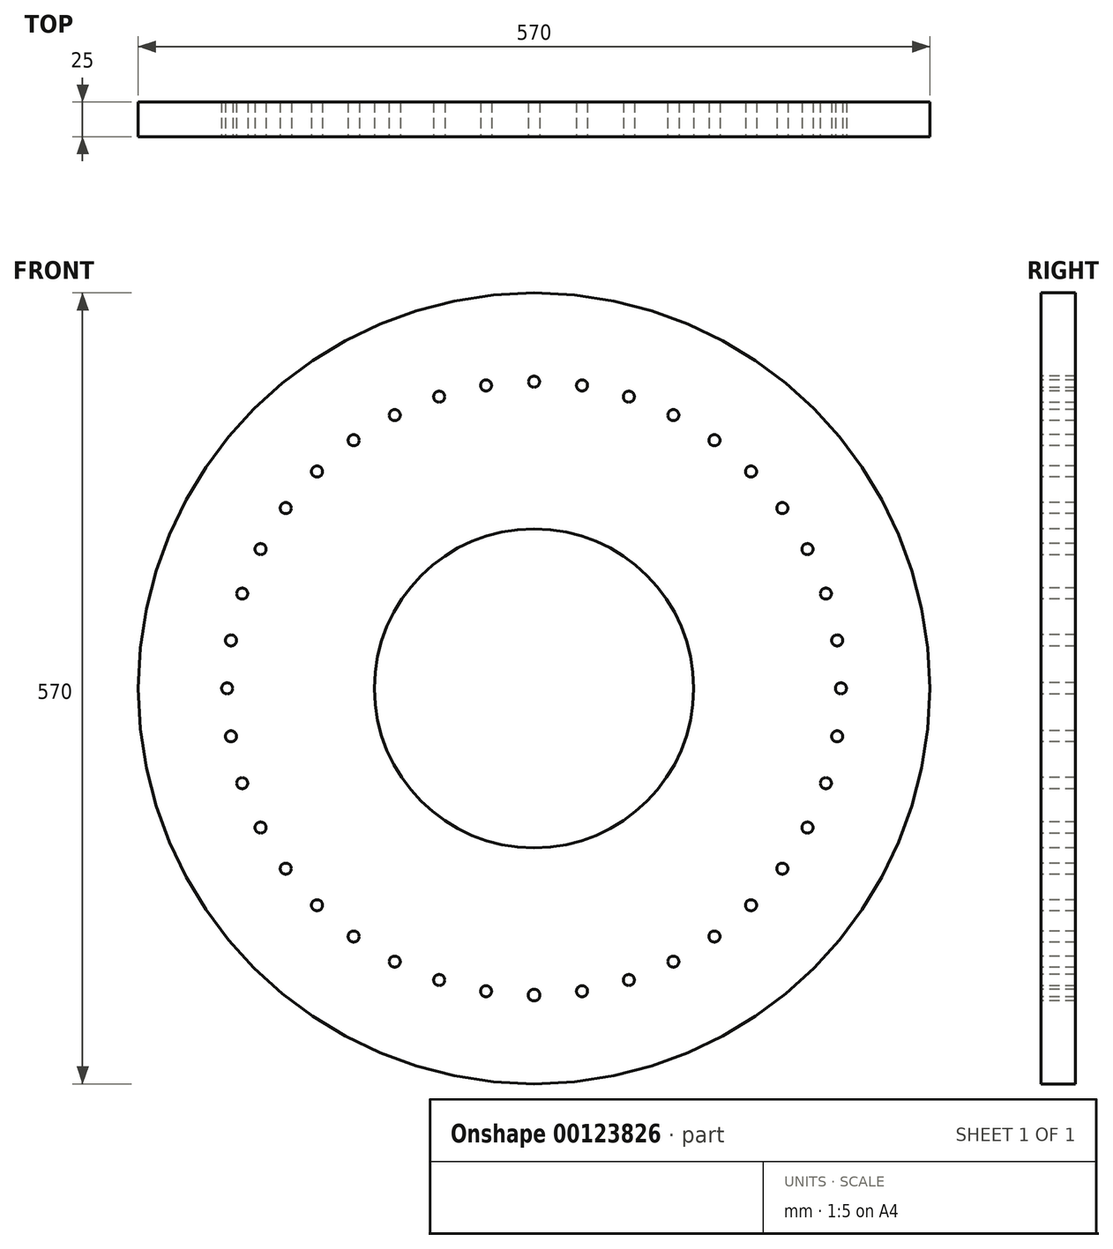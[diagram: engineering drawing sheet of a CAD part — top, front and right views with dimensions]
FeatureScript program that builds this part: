
annotation { "Feature Type Name" : "Feature", "Feature Type Description" : "" }
export const myFeature = defineFeature(function(context is Context, id is Id, definition is map)
    precondition{}
    {
        {
            var Q0;
            Q0=qCreatedBy(makeId("Front.planeOp"),FACE);
            var sketch = newSketch(context, id + "F0", { "sketchPlane" : qUnion([Q0])});
            skCircle(sketch, "E0", {"center": v(0, 0) * mm, "radius": 221 * mm, "construction": true});
            skLineSegment(sketch, "E1", {"start": v(0, 0) * mm, "end": v(0, 221) * mm, "construction": true});
            skLineSegment(sketch, "E2", {"start": v(0, 0) * mm, "end": v(-221, 0) * mm, "construction": true});
            skLineSegment(sketch, "E3", {"start": v(-218.28, 34.57) * mm, "end": v(0, 0) * mm, "construction": true});
            skLineSegment(sketch, "E4", {"start": v(-210.18, 68.3) * mm, "end": v(0, 0) * mm, "construction": true});
            skLineSegment(sketch, "E5", {"start": v(-178.8, 129.9) * mm, "end": v(0, 0) * mm, "construction": true});
            skLineSegment(sketch, "E6", {"start": v(-156.27, 156.27) * mm, "end": v(0, 0) * mm, "construction": true});
            skLineSegment(sketch, "E7", {"start": v(-129.9, 178.8) * mm, "end": v(0, 0) * mm, "construction": true});
            skLineSegment(sketch, "E8", {"start": v(-34.57, 218.28) * mm, "end": v(0, 0) * mm, "construction": true});
            skLineSegment(sketch, "E9", {"start": v(-68.3, 210.18) * mm, "end": v(0, 0) * mm, "construction": true});
            skLineSegment(sketch, "E10", {"start": v(-100.33, 196.91) * mm, "end": v(0, 0) * mm, "construction": true});
            skLineSegment(sketch, "E11", {"start": v(-196.91, 100.33) * mm, "end": v(0, 0) * mm, "construction": true});
            skCircle(sketch, "E12", {"center": v(-34.57, 218.28) * mm, "radius": 4 * mm});
            skCircle(sketch, "E13", {"center": v(-68.3, 210.18) * mm, "radius": 4 * mm});
            skCircle(sketch, "E14", {"center": v(-100.33, 196.91) * mm, "radius": 4 * mm});
            skCircle(sketch, "E15", {"center": v(-156.27, 156.27) * mm, "radius": 4 * mm});
            skCircle(sketch, "E16", {"center": v(-129.9, 178.8) * mm, "radius": 4 * mm});
            skCircle(sketch, "E17", {"center": v(-178.8, 129.9) * mm, "radius": 4 * mm});
            skCircle(sketch, "E18", {"center": v(-196.91, 100.33) * mm, "radius": 4 * mm});
            skCircle(sketch, "E19", {"center": v(-210.18, 68.3) * mm, "radius": 4 * mm});
            skCircle(sketch, "E20", {"center": v(-218.28, 34.57) * mm, "radius": 4 * mm});
            skCircle(sketch, "E21", {"center": v(-221, 0) * mm, "radius": 4 * mm});
            skCircle(sketch, "E22.MirrorC", {"center": v(100.33, 196.91) * mm, "radius": 4 * mm});
            skCircle(sketch, "E23.MirrorC", {"center": v(34.57, 218.28) * mm, "radius": 4 * mm});
            skCircle(sketch, "E24.MirrorC", {"center": v(68.3, 210.18) * mm, "radius": 4 * mm});
            skCircle(sketch, "E25.MirrorC", {"center": v(129.9, 178.8) * mm, "radius": 4 * mm});
            skCircle(sketch, "E26.MirrorC", {"center": v(178.8, 129.9) * mm, "radius": 4 * mm});
            skCircle(sketch, "E27.MirrorC", {"center": v(156.27, 156.27) * mm, "radius": 4 * mm});
            skCircle(sketch, "E28.MirrorC", {"center": v(218.28, 34.57) * mm, "radius": 4 * mm});
            skCircle(sketch, "E29.MirrorC", {"center": v(221, 0) * mm, "radius": 4 * mm});
            skCircle(sketch, "E30.MirrorC", {"center": v(210.18, 68.3) * mm, "radius": 4 * mm});
            skCircle(sketch, "E31.MirrorC", {"center": v(-100.33, -196.91) * mm, "radius": 4 * mm});
            skCircle(sketch, "E32.MirrorC", {"center": v(-68.3, -210.18) * mm, "radius": 4 * mm});
            skCircle(sketch, "E33.MirrorC", {"center": v(-196.91, -100.33) * mm, "radius": 4 * mm});
            skCircle(sketch, "E34.MirrorC", {"center": v(-34.57, -218.28) * mm, "radius": 4 * mm});
            skCircle(sketch, "E35.MirrorC", {"center": v(-218.28, -34.57) * mm, "radius": 4 * mm});
            skCircle(sketch, "E36.MirrorC", {"center": v(-129.9, -178.8) * mm, "radius": 4 * mm});
            skCircle(sketch, "E37.MirrorC", {"center": v(-210.18, -68.3) * mm, "radius": 4 * mm});
            skCircle(sketch, "E38.MirrorC", {"center": v(-178.8, -129.9) * mm, "radius": 4 * mm});
            skCircle(sketch, "E39.MirrorC", {"center": v(-156.27, -156.27) * mm, "radius": 4 * mm});
            skCircle(sketch, "E40.MirrorC", {"center": v(34.57, -218.28) * mm, "radius": 4 * mm});
            skCircle(sketch, "E41.MirrorC", {"center": v(178.8, -129.9) * mm, "radius": 4 * mm});
            skCircle(sketch, "E42.MirrorC", {"center": v(129.9, -178.8) * mm, "radius": 4 * mm});
            skCircle(sketch, "E43.MirrorC", {"center": v(156.27, -156.27) * mm, "radius": 4 * mm});
            skCircle(sketch, "E44.MirrorC", {"center": v(68.3, -210.18) * mm, "radius": 4 * mm});
            skCircle(sketch, "E45.MirrorC", {"center": v(100.33, -196.91) * mm, "radius": 4 * mm});
            skCircle(sketch, "E46.MirrorC", {"center": v(210.18, -68.3) * mm, "radius": 4 * mm});
            skCircle(sketch, "E47.MirrorC", {"center": v(218.28, -34.57) * mm, "radius": 4 * mm});
            skCircle(sketch, "E48.MirrorC", {"center": v(196.91, 100.33) * mm, "radius": 4 * mm});
            skCircle(sketch, "E49.MirrorC", {"center": v(196.91, -100.33) * mm, "radius": 4 * mm});
            skCircle(sketch, "E50", {"center": v(0, 0) * mm, "radius": 115 * mm});
            skLineSegment(sketch, "E51", {"start": v(0, 0) * mm, "end": v(19.07, 0) * mm, "construction": true});
            skCircle(sketch, "E52", {"center": v(0, 0) * mm, "radius": 285 * mm});
            skCircle(sketch, "E53", {"center": v(0, 221) * mm, "radius": 4 * mm});
            skCircle(sketch, "E54", {"center": v(0, -221) * mm, "radius": 4.26 * mm});
            skLineSegment(sketch, "E55", {"start": v(0, 0) * mm, "end": v(0, -221) * mm, "construction": true});
            skLineSegment(sketch, "E56", {"start": v(0, 0) * mm, "end": v(-34.57, -218.28) * mm, "construction": true});
            skLineSegment(sketch, "E57", {"start": v(0, 0) * mm, "end": v(-156.27, -156.27) * mm, "construction": true});
            skLineSegment(sketch, "E58", {"start": v(0, 0) * mm, "end": v(-129.9, -178.8) * mm, "construction": true});
            skSolve(sketch);
        }
        {
            var Q0;
            Q0=sQuery(id+"F0.wireOp",EDGE,"E52");
            var Q1;
            Q1=sQuery(id+"F0.wireOp",EDGE,"E50");
            var Q2;
            Q2=sQuery(id+"F0.wireOp",EDGE,"E42.MirrorC");
            var Q3;
            Q3=sQuery(id+"F0.wireOp",EDGE,"E26.MirrorC");
            var Q4;
            Q4=sQuery(id+"F0.wireOp",EDGE,"E35.MirrorC");
            var Q5;
            Q5=sQuery(id+"F0.wireOp",EDGE,"E43.MirrorC");
            var Q6;
            Q6=sQuery(id+"F0.wireOp",EDGE,"E27.MirrorC");
            var Q7;
            Q7=sQuery(id+"F0.wireOp",EDGE,"E23.MirrorC");
            var Q8;
            Q8=sQuery(id+"F0.wireOp",EDGE,"E45.MirrorC");
            var Q9;
            Q9=sQuery(id+"F0.wireOp",EDGE,"E29.MirrorC");
            var Q10;
            Q10=sQuery(id+"F0.wireOp",EDGE,"E48.MirrorC");
            var Q11;
            Q11=sQuery(id+"F0.wireOp",EDGE,"E32.MirrorC");
            var Q12;
            Q12=sQuery(id+"F0.wireOp",EDGE,"E44.MirrorC");
            var Q13;
            Q13=sQuery(id+"F0.wireOp",EDGE,"E28.MirrorC");
            var Q14;
            Q14=sQuery(id+"F0.wireOp",EDGE,"E40.MirrorC");
            var Q15;
            Q15=sQuery(id+"F0.wireOp",EDGE,"E24.MirrorC");
            var Q16;
            Q16=sQuery(id+"F0.wireOp",EDGE,"E46.MirrorC");
            var Q17;
            Q17=sQuery(id+"F0.wireOp",EDGE,"E37.MirrorC");
            var Q18;
            Q18=sQuery(id+"F0.wireOp",EDGE,"E30.MirrorC");
            var Q19;
            Q19=sQuery(id+"F0.wireOp",EDGE,"E49.MirrorC");
            var Q20;
            Q20=sQuery(id+"F0.wireOp",EDGE,"E33.MirrorC");
            var Q21;
            Q21=sQuery(id+"F0.wireOp",EDGE,"E41.MirrorC");
            var Q22;
            Q22=sQuery(id+"F0.wireOp",EDGE,"E25.MirrorC");
            var Q23;
            Q23=sQuery(id+"F0.wireOp",EDGE,"E22.MirrorC");
            var Q24;
            Q24=sQuery(id+"F0.wireOp",EDGE,"E47.MirrorC");
            var Q25;
            Q25=sQuery(id+"F0.wireOp",EDGE,"E31.MirrorC");
            var Q26;
            Q26=sQuery(id+"F0.wireOp",EDGE,"E38.MirrorC");
            var Q27;
            Q27=sQuery(id+"F0.wireOp",EDGE,"E19");
            var Q28;
            Q28=sQuery(id+"F0.wireOp",EDGE,"E13");
            var Q29;
            Q29=sQuery(id+"F0.wireOp",EDGE,"E14");
            var Q30;
            Q30=sQuery(id+"F0.wireOp",EDGE,"E15");
            var Q31;
            Q31=sQuery(id+"F0.wireOp",EDGE,"E12");
            var Q32;
            Q32=sQuery(id+"F0.wireOp",EDGE,"E39.MirrorC");
            var Q33;
            Q33=sQuery(id+"F0.wireOp",EDGE,"E20");
            var Q34;
            Q34=sQuery(id+"F0.wireOp",EDGE,"E36.MirrorC");
            var Q35;
            Q35=sQuery(id+"F0.wireOp",EDGE,"E16");
            var Q36;
            Q36=sQuery(id+"F0.wireOp",EDGE,"E21");
            var Q37;
            Q37=sQuery(id+"F0.wireOp",EDGE,"E53");
            var Q38;
            Q38=sQuery(id+"F0.wireOp",EDGE,"E17");
            var Q39;
            Q39=sQuery(id+"F0.wireOp",EDGE,"E54");
            var Q40;
            Q40=sQuery(id+"F0.wireOp",EDGE,"E18");
            var Q41;
            Q41=sQuery(id+"F0.wireOp",EDGE,"E34.MirrorC");
            extrude(context, id + "F1", {"bodyType" : ToolBodyType.SURFACE, "surfaceEntities" : qUnion([Q0, Q1, Q2, Q3, Q4, Q5, Q6, Q7, Q8, Q9, Q10, Q11, Q12, Q13, Q14, Q15, Q16, Q17, Q18, Q19, Q20, Q21, Q22, Q23, Q24, Q25, Q26, Q27, Q28, Q29, Q30, Q31, Q32, Q33, Q34, Q35, Q36, Q37, Q38, Q39, Q40, Q41]), "depth" : 25 * mm});
        }
    });
